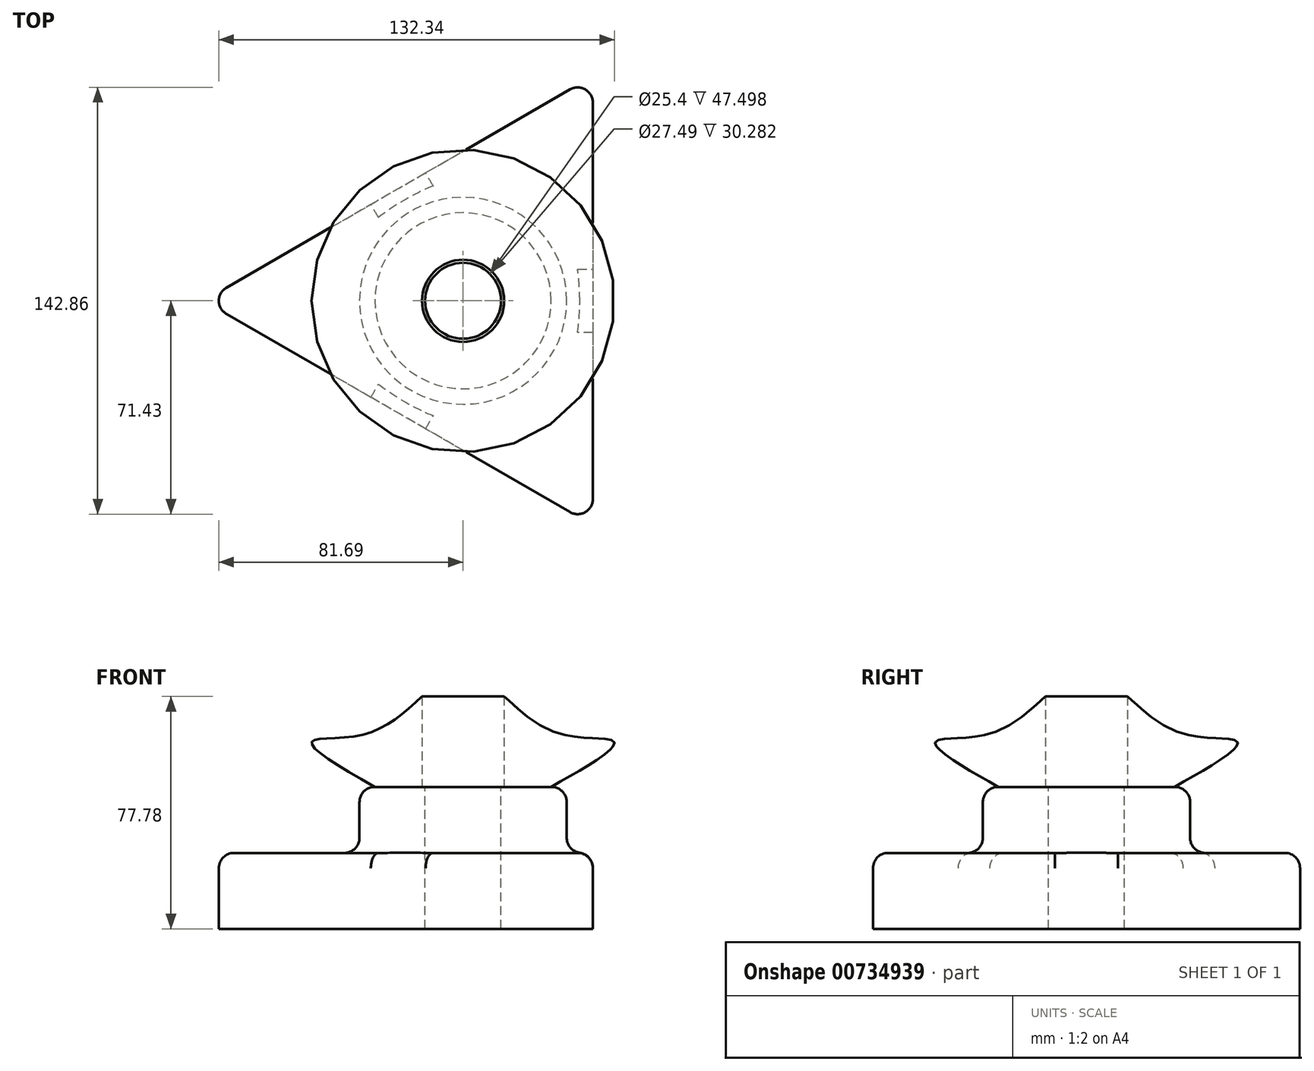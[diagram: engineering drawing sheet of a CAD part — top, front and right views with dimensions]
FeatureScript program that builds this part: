
annotation { "Feature Type Name" : "Feature", "Feature Type Description" : "" }
export const myFeature = defineFeature(function(context is Context, id is Id, definition is map)
    precondition{}
    {
        {
            var Q0;
            Q0=qCreatedBy(makeId("Top.planeOp"),FACE);
            var sketch = newSketch(context, id + "F0", { "sketchPlane" : qUnion([Q0])});
            skCircle(sketch, "E0.cCircle", {"center": v(0, 0) * mm, "radius": 43.39 * mm, "construction": true});
            skLineSegment(sketch, "E0.0", {"start": v(43.39, 75.15) * mm, "end": v(43.39, -75.15) * mm});
            skLineSegment(sketch, "E0.1", {"start": v(43.39, -75.15) * mm, "end": v(-86.77, 0) * mm});
            skLineSegment(sketch, "E0.2", {"start": v(-86.77, 0) * mm, "end": v(43.39, 75.15) * mm});
            skPoint(sketch, "E0.0.midPoint", {"position": v(43.39, 0) * mm});
            skSolve(sketch);
        }
        {
            var Q0;
            Q0=makeQuery(id+"F0.imprint","IMPRINT",FACE,{"disambiguationData":[TD([[makeQuery(id+"F0.imprint","IMPRINT",EDGE,{"derivedFrom":sQuery(id+"F0.wireOp",EDGE,"E0.0")}),-1.0]])]});
            extrude(context, id + "F1", {"entities" : qUnion([Q0]), "depth" : 25.4 * mm, "offsetDistance" : 25.4 * mm});
        }
        {
            var Q0;
            Q0=qCreatedBy(makeId("Top.planeOp"),FACE);
            var sketch = newSketch(context, id + "F2", { "sketchPlane" : qUnion([Q0])});
            skCircle(sketch, "E1", {"center": v(0, 0) * mm, "radius": 34.66 * mm});
            skSolve(sketch);
        }
        {
            var Q0;
            Q0=makeQuery(id+"F2.imprint","IMPRINT",FACE,{"disambiguationData":[TD([[makeQuery(id+"F2.imprint","IMPRINT",EDGE,{"derivedFrom":sQuery(id+"F2.wireOp",EDGE,"E1")}),1.0]])]});
            extrude(context, id + "F3", {"entities" : qUnion([Q0]), "operationType" : NewBodyOperationType.ADD, "depth" : 47.5 * mm, "offsetDistance" : 25.4 * mm});
        }
        {
            var Q0;
            Q0=makeQuery(id+"F3.boolean.opBoolean","INTERSECT",EDGE,{"derivedFrom":[makeQuery(id+"F1.opExtrude","CAP_FACE",FACE,{"disambiguationData":[OSD([sQuery(id+"F0.wireOp",EDGE,"E0.0"),sQuery(id+"F0.wireOp",EDGE,"E0.1"),sQuery(id+"F0.wireOp",EDGE,"E0.2")])],"isStart":false}),makeQuery(id+"F3.opExtrude","SWEPT_FACE",FACE,{"disambiguationData":[OSD([sQuery(id+"F2.wireOp",EDGE,"E1")])]})]});
            var Q1;
            Q1=makeQuery(id+"F3.opExtrude","CAP_FACE",FACE,{"disambiguationData":[OSD([sQuery(id+"F2.wireOp",EDGE,"E1")])],"isStart":false});
            fillet(context, id + "F4", {"entities" : qUnion([Q0, Q1]), "radius" : 5.08 * mm, "tangentPropagation" : true, "allowEdgeOverflow" : false});
        }
        {
            var Q0;
            Q0=makeQuery(id+"F3.opExtrude","CAP_FACE",FACE,{"disambiguationData":[OSD([sQuery(id+"F2.wireOp",EDGE,"E1")])],"isStart":false});
            var sketch = newSketch(context, id + "F5", { "sketchPlane" : qUnion([Q0])});
            skCircle(sketch, "E2", {"center": v(0, 0) * mm, "radius": 12.7 * mm});
            skSolve(sketch);
        }
        {
            var Q0;
            Q0=makeQuery(id+"F5.imprint","IMPRINT",FACE,{"disambiguationData":[TD([[makeQuery(id+"F5.imprint","IMPRINT",EDGE,{"derivedFrom":sQuery(id+"F5.wireOp",EDGE,"E2")}),1.0]])]});
            extrude(context, id + "F6", {"entities" : qUnion([Q0]), "operationType" : NewBodyOperationType.REMOVE, "endBound" : BoundingType.THROUGH_ALL, "oppositeDirection" : true, "depth" : 25.4 * mm, "offsetDistance" : 25.4 * mm});
        }
        {
            var Q0;
            Q0=makeQuery(id+"F1.opExtrude","CAP_EDGE",EDGE,{"disambiguationData":[OSD([sQuery(id+"F0.wireOp",EDGE,"E0.0")])],"isStart":false});
            var Q1;
            Q1=makeQuery(id+"F1.opExtrude","CAP_EDGE",EDGE,{"disambiguationData":[OSD([sQuery(id+"F0.wireOp",EDGE,"E0.1")])],"isStart":false});
            var Q2;
            Q2=makeQuery(id+"F1.opExtrude","CAP_EDGE",EDGE,{"disambiguationData":[OSD([sQuery(id+"F0.wireOp",EDGE,"E0.2")])],"isStart":false});
            var Q3;
            Q3=makeQuery(id+"F1.opExtrude","SWEPT_EDGE",EDGE,{"disambiguationData":[OSD([sQuery(id+"F0.wireOp",EDGE,"E0.0"),sQuery(id+"F0.wireOp",EDGE,"E0.1")])]});
            var Q4;
            Q4=makeQuery(id+"F1.opExtrude","SWEPT_EDGE",EDGE,{"disambiguationData":[OSD([sQuery(id+"F0.wireOp",EDGE,"E0.0"),sQuery(id+"F0.wireOp",EDGE,"E0.2")])]});
            var Q5;
            Q5=makeQuery(id+"F1.opExtrude","SWEPT_EDGE",EDGE,{"disambiguationData":[OSD([sQuery(id+"F0.wireOp",EDGE,"E0.1"),sQuery(id+"F0.wireOp",EDGE,"E0.2")])]});
            fillet(context, id + "F7", {"entities" : qUnion([Q0, Q1, Q2, Q3, Q4, Q5]), "radius" : 5.08 * mm, "tangentPropagation" : true, "allowEdgeOverflow" : false});
        }
        {
            var Q0;
            Q0=qCreatedBy(makeId("Right.planeOp"),FACE);
            var sketch = newSketch(context, id + "F8", { "sketchPlane" : qUnion([Q0])});
            skLineSegment(sketch, "E3", {"start": v(0, 0) * mm, "end": v(0, 74.61) * mm});
            skLineSegment(sketch, "E4", {"start": v(13.74, 0) * mm, "end": v(13.74, 77.78) * mm});
            skFitSpline(sketch, "E5", {"points": [v(13.74, 77.78) * mm, v(34.18, 64.83) * mm, v(50.58, 62.53) * mm, v(13.74, 38.89) * mm], "startDerivative": vector(57.23, -52.87) * mm, "endDerivative": vector(-135.2, -73.3) * mm});
            skSolve(sketch);
        }
        {
            var Q0;
            {var subQ0=sQuery(id+"F8.wireOp",EDGE,"E5");Q0=makeQuery(id+"F8.imprint","IMPRINT",FACE,{"disambiguationData":[TD([[makeQuery(id+"F8.imprint","IMPRINT",EDGE,{"derivedFrom":subQ0}),-1.0]])]});}
            var Q1;
            Q1=sQuery(id+"F8.wireOp",EDGE,"E3");
            revolve(context, id + "F9", {"operationType" : NewBodyOperationType.ADD, "surfaceOperationType" : NewSurfaceOperationType.NEW, "entities" : qUnion([Q0]), "axis" : qUnion([Q1]), "revolveType" : RevolveType.FULL});
        }
    });
